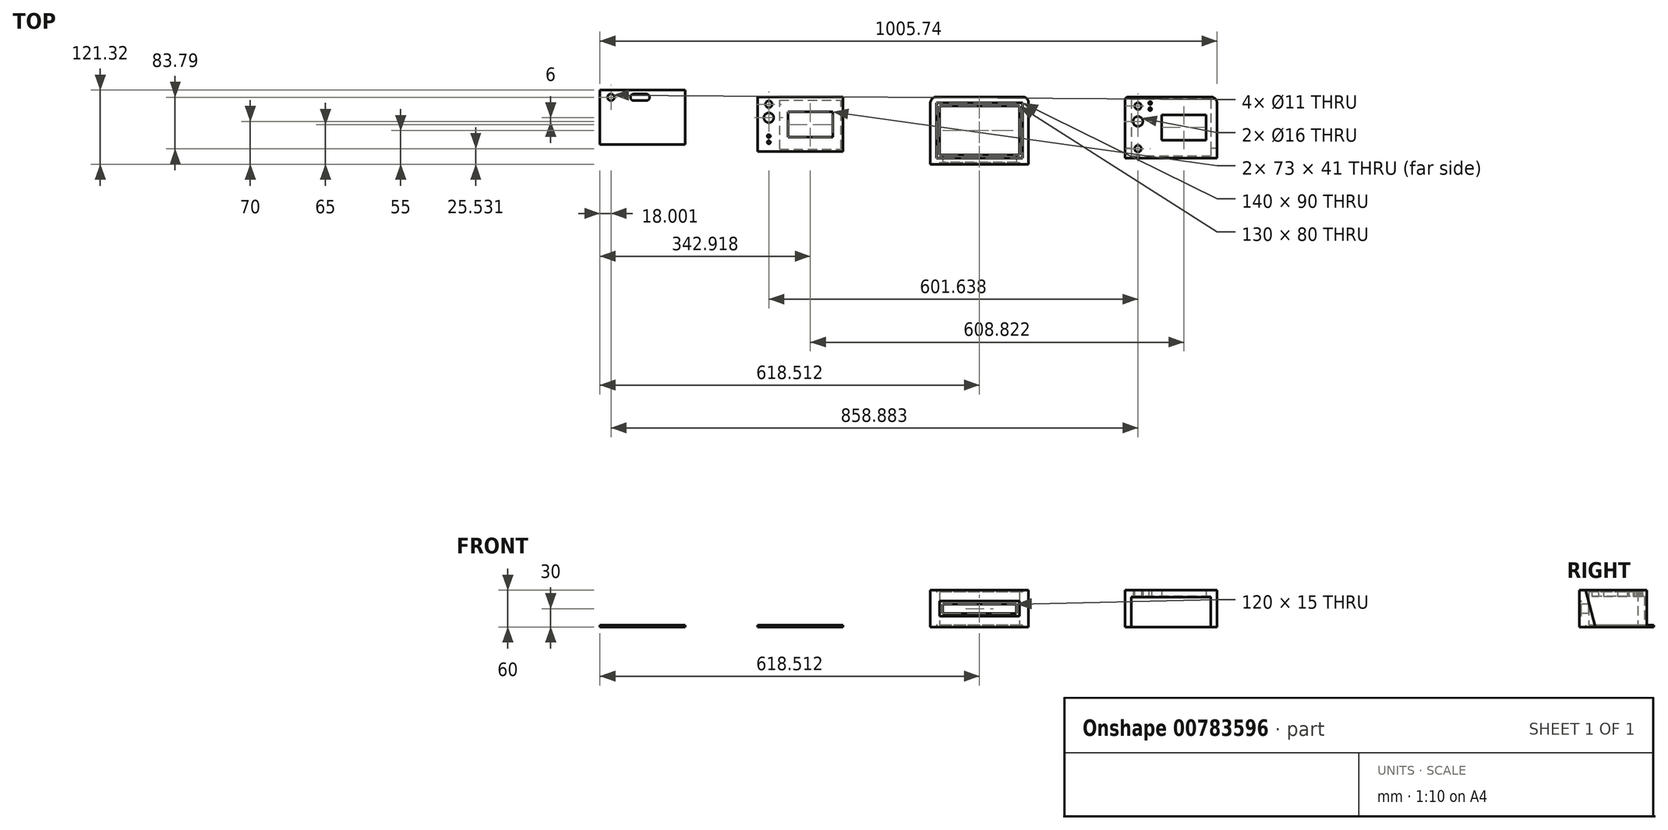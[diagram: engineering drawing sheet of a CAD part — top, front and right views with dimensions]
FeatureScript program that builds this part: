
annotation { "Feature Type Name" : "Feature", "Feature Type Description" : "" }
export const myFeature = defineFeature(function(context is Context, id is Id, definition is map)
    precondition{}
    {
        {
            var Q0;
            Q0=qCreatedBy(makeId("Top.planeOp"),FACE);
            var sketch = newSketch(context, id + "F0", { "sketchPlane" : qUnion([Q0])});
            skLineSegment(sketch, "E0.bottom", {"start": v(5, 0) * mm, "end": v(140, 0) * mm});
            skLineSegment(sketch, "E0.top", {"start": v(0, -100) * mm, "end": v(150, -100) * mm});
            skLineSegment(sketch, "E0.left", {"start": v(0, -5) * mm, "end": v(0, -100) * mm});
            skLineSegment(sketch, "E0.right", {"start": v(150, -10) * mm, "end": v(150, -100) * mm});
            skLineSegment(sketch, "E1.bottom", {"start": v(59.5, -70.5) * mm, "end": v(132.5, -70.5) * mm});
            skLineSegment(sketch, "E1.top", {"start": v(59.5, -29.5) * mm, "end": v(132.5, -29.5) * mm});
            skLineSegment(sketch, "E1.left", {"start": v(59.5, -70.5) * mm, "end": v(59.5, -29.5) * mm});
            skLineSegment(sketch, "E1.right", {"start": v(132.5, -70.5) * mm, "end": v(132.5, -29.5) * mm});
            skPoint(sketch, "E1.middle", {"position": v(96, -50) * mm});
            skLineSegment(sketch, "E2.bottom", {"start": v(46, -90) * mm, "end": v(146, -90) * mm, "construction": true});
            skLineSegment(sketch, "E2.top", {"start": v(46, -10) * mm, "end": v(146, -10) * mm, "construction": true});
            skLineSegment(sketch, "E2.left", {"start": v(46, -90) * mm, "end": v(46, -10) * mm, "construction": true});
            skLineSegment(sketch, "E2.right", {"start": v(146, -90) * mm, "end": v(146, -10) * mm, "construction": true});
            skLineSegment(sketch, "E3", {"start": v(21.14, 0) * mm, "end": v(21.14, -100) * mm, "construction": true});
            skLineSegment(sketch, "E4", {"start": v(41, 0) * mm, "end": v(41, -100) * mm, "construction": true});
            skCircle(sketch, "E5", {"center": v(41, -10) * mm, "radius": 2.5 * mm});
            skCircle(sketch, "E6", {"center": v(41, -20) * mm, "radius": 2.5 * mm});
            skCircle(sketch, "E7", {"center": v(21.14, -15) * mm, "radius": 5.5 * mm});
            skCircle(sketch, "E8", {"center": v(21.14, -84.47) * mm, "radius": 5.5 * mm});
            skCircle(sketch, "E9", {"center": v(21.14, -40) * mm, "radius": 8 * mm});
            skPoint(sketch, "E10.visualSharp", {"position": v(0, 0) * mm});
            skArc(sketch, "E10.filletArc", {"start": v(5, 0) * mm, "mid": v(1.46, -1.46) * mm, "end": v(0, -5) * mm});
            skPoint(sketch, "E11.visualSharp", {"position": v(150, 0) * mm});
            skArc(sketch, "E11.filletArc", {"start": v(150, -10) * mm, "mid": v(147.07, -2.93) * mm, "end": v(140, 0) * mm});
            skSolve(sketch);
        }
        {
            var Q0;
            Q0=makeQuery(id+"F0.imprint","IMPRINT",FACE,{"disambiguationData":[TD([[makeQuery(id+"F0.imprint","IMPRINT",EDGE,{"derivedFrom":sQuery(id+"F0.wireOp",EDGE,"E0.bottom")}),-1.0]])]});
            extrude(context, id + "F1", {"entities" : qUnion([Q0]), "depth" : 60 * mm, "offsetDistance" : 25 * mm});
        }
        {
            var Q0;
            Q0=makeQuery(id+"F1.opExtrude","CAP_FACE",FACE,{"disambiguationData":[OSD([sQuery(id+"F0.wireOp",EDGE,"E0.bottom"),sQuery(id+"F0.wireOp",EDGE,"E0.top"),sQuery(id+"F0.wireOp",EDGE,"E0.left"),sQuery(id+"F0.wireOp",EDGE,"E0.right"),sQuery(id+"F0.wireOp",EDGE,"E1.bottom"),sQuery(id+"F0.wireOp",EDGE,"E1.top"),sQuery(id+"F0.wireOp",EDGE,"E1.left"),sQuery(id+"F0.wireOp",EDGE,"E1.right"),sQuery(id+"F0.wireOp",EDGE,"E5"),sQuery(id+"F0.wireOp",EDGE,"E6"),sQuery(id+"F0.wireOp",EDGE,"E7"),sQuery(id+"F0.wireOp",EDGE,"E8"),sQuery(id+"F0.wireOp",EDGE,"E9")])],"isStart":true});
            var sketch = newSketch(context, id + "F2", { "sketchPlane" : qUnion([Q0])});
            skLineSegment(sketch, "E12.bottom", {"start": v(140, 4) * mm, "end": v(10, 4) * mm});
            skLineSegment(sketch, "E12.top", {"start": v(140, 97) * mm, "end": v(10, 97) * mm});
            skLineSegment(sketch, "E12.left", {"start": v(140, 4) * mm, "end": v(140, 97) * mm});
            skLineSegment(sketch, "E12.right", {"start": v(10, 4) * mm, "end": v(10, 97) * mm});
            skSolve(sketch);
        }
        {
            var Q0;
            Q0=makeQuery(id+"F2.imprint","IMPRINT",FACE,{"disambiguationData":[TD([[makeQuery(id+"F2.imprint","IMPRINT",EDGE,{"derivedFrom":sQuery(id+"F2.wireOp",EDGE,"E12.bottom")}),-1.0]])]});
            extrude(context, id + "F3", {"entities" : qUnion([Q0]), "operationType" : NewBodyOperationType.REMOVE, "oppositeDirection" : true, "depth" : 50 * mm, "offsetDistance" : 25 * mm});
        }
        {
            var Q0;
            Q0=makeQuery(id+"F1.opExtrude","SWEPT_FACE",FACE,{"disambiguationData":[OSD([sQuery(id+"F0.wireOp",EDGE,"E0.left")])]});
            var sketch = newSketch(context, id + "F4", { "sketchPlane" : qUnion([Q0])});
            skLineSegment(sketch, "E13", {"start": v(100, 60) * mm, "end": v(83.92, 0) * mm});
            skSolve(sketch);
        }
        {
            var Q0;
            {var subQ0=sQuery(id+"F4.wireOp",EDGE,"E13");Q0=makeQuery(id+"F4.imprint","IMPRINT",FACE,{"disambiguationData":[TD([[makeQuery(id+"F4.imprint","IMPRINT",EDGE,{"derivedFrom":subQ0}),1.0]])]});}
            extrude(context, id + "F5", {"entities" : qUnion([Q0]), "operationType" : NewBodyOperationType.REMOVE, "endBound" : BoundingType.THROUGH_ALL, "oppositeDirection" : true, "depth" : 25 * mm, "offsetDistance" : 25 * mm});
        }
        {
            var Q0;
            Q0=qCreatedBy(makeId("Top.planeOp"),FACE);
            var sketch = newSketch(context, id + "F6", { "sketchPlane" : qUnion([Q0])});
            skLineSegment(sketch, "E14.bottom", {"start": v(-157.23, 0) * mm, "end": v(-317.23, 0) * mm});
            skLineSegment(sketch, "E14.top", {"start": v(-157.23, -110) * mm, "end": v(-317.23, -110) * mm});
            skLineSegment(sketch, "E14.left", {"start": v(-157.23, 0) * mm, "end": v(-157.23, -110) * mm});
            skLineSegment(sketch, "E14.right", {"start": v(-317.23, 0) * mm, "end": v(-317.23, -110) * mm});
            skLineSegment(sketch, "E15.0", {"start": v(-167.23, -10) * mm, "end": v(-307.23, -10) * mm});
            skLineSegment(sketch, "E15.1", {"start": v(-167.23, -10) * mm, "end": v(-167.23, -100) * mm});
            skLineSegment(sketch, "E15.2", {"start": v(-167.23, -100) * mm, "end": v(-307.23, -100) * mm});
            skLineSegment(sketch, "E15.3", {"start": v(-307.23, -10) * mm, "end": v(-307.23, -100) * mm});
            skLineSegment(sketch, "E16.0", {"start": v(-302.23, -15) * mm, "end": v(-302.23, -95) * mm});
            skLineSegment(sketch, "E16.1", {"start": v(-172.23, -15) * mm, "end": v(-302.23, -15) * mm});
            skLineSegment(sketch, "E16.2", {"start": v(-172.23, -15) * mm, "end": v(-172.23, -95) * mm});
            skLineSegment(sketch, "E16.3", {"start": v(-172.23, -95) * mm, "end": v(-302.23, -95) * mm});
            skSolve(sketch);
        }
        {
            var Q0;
            Q0=makeQuery(id+"F6.imprint","IMPRINT",FACE,{"disambiguationData":[TD([[makeQuery(id+"F6.imprint","IMPRINT",EDGE,{"derivedFrom":sQuery(id+"F6.wireOp",EDGE,"E14.bottom")}),1.0]])]});
            extrude(context, id + "F7", {"entities" : qUnion([Q0]), "depth" : 60 * mm, "offsetDistance" : 25 * mm});
        }
        {
            var Q0;
            Q0=makeQuery(id+"F7.opExtrude","SWEPT_EDGE",EDGE,{"disambiguationData":[OSD([sQuery(id+"F6.wireOp",EDGE,"E14.bottom"),sQuery(id+"F6.wireOp",EDGE,"E14.right")])]});
            var Q1;
            Q1=makeQuery(id+"F7.opExtrude","SWEPT_EDGE",EDGE,{"disambiguationData":[OSD([sQuery(id+"F6.wireOp",EDGE,"E14.bottom"),sQuery(id+"F6.wireOp",EDGE,"E14.left")])]});
            fillet(context, id + "F8", {"entities" : qUnion([Q0, Q1]), "radius" : 10 * mm, "tangentPropagation" : true, "allowEdgeOverflow" : false});
        }
        {
            var Q0;
            Q0=makeQuery(id+"F6.imprint","IMPRINT",FACE,{"disambiguationData":[TD([[makeQuery(id+"F6.imprint","IMPRINT",EDGE,{"derivedFrom":sQuery(id+"F6.wireOp",EDGE,"E15.0")}),1.0]])]});
            extrude(context, id + "F9", {"entities" : qUnion([Q0]), "operationType" : NewBodyOperationType.ADD, "depth" : 57 * mm, "offsetDistance" : 25 * mm});
        }
        {
            var Q0;
            Q0=makeQuery(id+"F7.opExtrude","SWEPT_FACE",FACE,{"disambiguationData":[OSD([sQuery(id+"F6.wireOp",EDGE,"E14.top")])]});
            var sketch = newSketch(context, id + "F10", { "sketchPlane" : qUnion([Q0])});
            skLineSegment(sketch, "E17.bottom", {"start": v(-177.23, 22.5) * mm, "end": v(-297.23, 22.5) * mm});
            skLineSegment(sketch, "E17.top", {"start": v(-177.23, 37.5) * mm, "end": v(-297.23, 37.5) * mm});
            skLineSegment(sketch, "E17.left", {"start": v(-177.23, 22.5) * mm, "end": v(-177.23, 37.5) * mm});
            skLineSegment(sketch, "E17.right", {"start": v(-297.23, 22.5) * mm, "end": v(-297.23, 37.5) * mm});
            skPoint(sketch, "E17.middle", {"position": v(-237.23, 30) * mm});
            skPoint(sketch, "E17.middle.positionSnap0", {"position": v(-237.23, 60) * mm});
            skPoint(sketch, "E17.centerSnap0", {"position": v(-237.23, 60) * mm});
            skLineSegment(sketch, "E18.bottom", {"start": v(-302.23, 17.5) * mm, "end": v(-172.23, 17.5) * mm});
            skLineSegment(sketch, "E18.top", {"start": v(-302.23, 42.5) * mm, "end": v(-172.23, 42.5) * mm});
            skLineSegment(sketch, "E18.left", {"start": v(-302.23, 17.5) * mm, "end": v(-302.23, 42.5) * mm});
            skLineSegment(sketch, "E18.right", {"start": v(-172.23, 17.5) * mm, "end": v(-172.23, 42.5) * mm});
            skSolve(sketch);
        }
        {
            var Q0;
            Q0=makeQuery(id+"F10.imprint","IMPRINT",FACE,{"disambiguationData":[TD([[makeQuery(id+"F10.imprint","IMPRINT",EDGE,{"derivedFrom":sQuery(id+"F10.wireOp",EDGE,"E17.bottom")}),-1.0]])]});
            extrude(context, id + "F11", {"entities" : qUnion([Q0]), "operationType" : NewBodyOperationType.REMOVE, "oppositeDirection" : true, "depth" : 15 * mm, "offsetDistance" : 25 * mm});
        }
        {
            var Q0;
            Q0=makeQuery(id+"F6.imprint","IMPRINT",FACE,{"disambiguationData":[TD([[makeQuery(id+"F6.imprint","IMPRINT",EDGE,{"derivedFrom":sQuery(id+"F6.wireOp",EDGE,"E15.0")}),1.0]])]});
            extrude(context, id + "F12", {"entities" : qUnion([Q0]), "operationType" : NewBodyOperationType.REMOVE, "depth" : 3 * mm, "offsetDistance" : 25 * mm});
        }
        {
            var Q0;
            Q0=qCreatedBy(makeId("Top.planeOp"),FACE);
            var sketch = newSketch(context, id + "F13", { "sketchPlane" : qUnion([Q0])});
            skLineSegment(sketch, "E19.bottom", {"start": v(-459.5, 0) * mm, "end": v(-598.5, 0) * mm});
            skLineSegment(sketch, "E19.top", {"start": v(-459.5, -89) * mm, "end": v(-598.5, -89) * mm});
            skLineSegment(sketch, "E19.left", {"start": v(-459.5, 0) * mm, "end": v(-459.5, -89) * mm});
            skLineSegment(sketch, "E19.right", {"start": v(-598.5, 0) * mm, "end": v(-598.5, -89) * mm});
            skLineSegment(sketch, "E20.bottom", {"start": v(-549.32, -65.5) * mm, "end": v(-476.32, -65.5) * mm});
            skLineSegment(sketch, "E20.top", {"start": v(-549.32, -24.5) * mm, "end": v(-476.32, -24.5) * mm});
            skLineSegment(sketch, "E20.left", {"start": v(-549.32, -65.5) * mm, "end": v(-549.32, -24.5) * mm});
            skLineSegment(sketch, "E20.right", {"start": v(-476.32, -65.5) * mm, "end": v(-476.32, -24.5) * mm});
            skPoint(sketch, "E20.middle", {"position": v(-512.82, -45) * mm});
            skLineSegment(sketch, "E21.bottom", {"start": v(-562.82, -85) * mm, "end": v(-462.82, -85) * mm});
            skLineSegment(sketch, "E21.top", {"start": v(-562.82, -5) * mm, "end": v(-462.82, -5) * mm});
            skLineSegment(sketch, "E21.left", {"start": v(-562.82, -85) * mm, "end": v(-562.82, -5) * mm});
            skLineSegment(sketch, "E21.right", {"start": v(-462.82, -85) * mm, "end": v(-462.82, -5) * mm});
            skLineSegment(sketch, "E22", {"start": v(-580.5, 6) * mm, "end": v(-580.5, -94) * mm, "construction": true});
            skLineSegment(sketch, "E23", {"start": v(-567.82, 5) * mm, "end": v(-567.82, -95) * mm, "construction": true});
            skCircle(sketch, "E24", {"center": v(-580.5, -12) * mm, "radius": 5.5 * mm});
            skCircle(sketch, "E25", {"center": v(-580.5, -74) * mm, "radius": 2.55 * mm});
            skCircle(sketch, "E26", {"center": v(-580.5, -34) * mm, "radius": 8 * mm});
            skPoint(sketch, "E27.visualSharp", {"position": v(-458.82, 5) * mm});
            skCircle(sketch, "E28", {"center": v(-580.5, -64) * mm, "radius": 2.55 * mm});
            skSolve(sketch);
        }
        {
            var Q0;
            Q0=makeQuery(id+"F13.imprint","IMPRINT",FACE,{"disambiguationData":[TD([[makeQuery(id+"F13.imprint","IMPRINT",EDGE,{"derivedFrom":sQuery(id+"F13.wireOp",EDGE,"E19.bottom")}),1.0]])]});
            var Q1;
            Q1=makeQuery(id+"F13.imprint","IMPRINT",FACE,{"disambiguationData":[TD([[makeQuery(id+"F13.imprint","IMPRINT",EDGE,{"derivedFrom":sQuery(id+"F13.wireOp",EDGE,"E20.bottom")}),-1.0]])]});
            extrude(context, id + "F14", {"entities" : qUnion([Q0, Q1]), "depth" : 3 * mm, "offsetDistance" : 25 * mm});
        }
        {
            var Q0;
            Q0=makeQuery(id+"F10.imprint","IMPRINT",FACE,{"disambiguationData":[TD([[makeQuery(id+"F10.imprint","IMPRINT",EDGE,{"derivedFrom":sQuery(id+"F10.wireOp",EDGE,"E17.bottom")}),1.0]])]});
            extrude(context, id + "F15", {"entities" : qUnion([Q0]), "operationType" : NewBodyOperationType.REMOVE, "oppositeDirection" : true, "depth" : 3 * mm, "offsetDistance" : 25 * mm});
        }
        {
            var Q0;
            Q0=makeQuery(id+"F13.imprint","IMPRINT",FACE,{"disambiguationData":[TD([[makeQuery(id+"F13.imprint","IMPRINT",EDGE,{"derivedFrom":sQuery(id+"F13.wireOp",EDGE,"E20.bottom")}),-1.0]])]});
            extrude(context, id + "F16", {"entities" : qUnion([Q0]), "operationType" : NewBodyOperationType.REMOVE, "depth" : 1 * mm, "offsetDistance" : 25 * mm});
        }
        {
            var Q0;
            Q0=qCreatedBy(makeId("Top.planeOp"),FACE);
            var sketch = newSketch(context, id + "F17", { "sketchPlane" : qUnion([Q0])});
            skLineSegment(sketch, "E29.bottom", {"start": v(-716.74, 11.32) * mm, "end": v(-855.74, 11.32) * mm});
            skLineSegment(sketch, "E29.top", {"start": v(-716.74, -77.68) * mm, "end": v(-855.74, -77.68) * mm});
            skLineSegment(sketch, "E29.left", {"start": v(-716.74, 11.32) * mm, "end": v(-716.74, -77.68) * mm});
            skLineSegment(sketch, "E29.right", {"start": v(-855.74, 11.32) * mm, "end": v(-855.74, -77.68) * mm});
            skPoint(sketch, "E30.middle", {"position": v(-770.07, -32.68) * mm});
            skLineSegment(sketch, "E31", {"start": v(-837.74, 17.32) * mm, "end": v(-837.74, -82.68) * mm, "construction": true});
            skLineSegment(sketch, "E32", {"start": v(-825.07, 17.32) * mm, "end": v(-825.07, -82.68) * mm, "construction": true});
            skCircle(sketch, "E33", {"center": v(-837.74, -0.68) * mm, "radius": 5.5 * mm});
            skCircle(sketch, "E34", {"center": v(-800.42, -0.68) * mm, "radius": 5.5 * mm});
            skCircle(sketch, "E35", {"center": v(-780.4, -0.68) * mm, "radius": 5.5 * mm});
            skLineSegment(sketch, "E36", {"start": v(-780.4, 4.82) * mm, "end": v(-800.42, 4.82) * mm});
            skLineSegment(sketch, "E37", {"start": v(-780.4, -6.18) * mm, "end": v(-800.42, -6.18) * mm});
            skSolve(sketch);
        }
        {
            var Q0;
            Q0=makeQuery(id+"F17.imprint","IMPRINT",FACE,{"disambiguationData":[TD([[makeQuery(id+"F17.imprint","IMPRINT",EDGE,{"derivedFrom":sQuery(id+"F17.wireOp",EDGE,"E29.bottom")}),1.0]])]});
            extrude(context, id + "F18", {"entities" : qUnion([Q0]), "depth" : 3 * mm, "offsetDistance" : 25 * mm});
        }
    });
